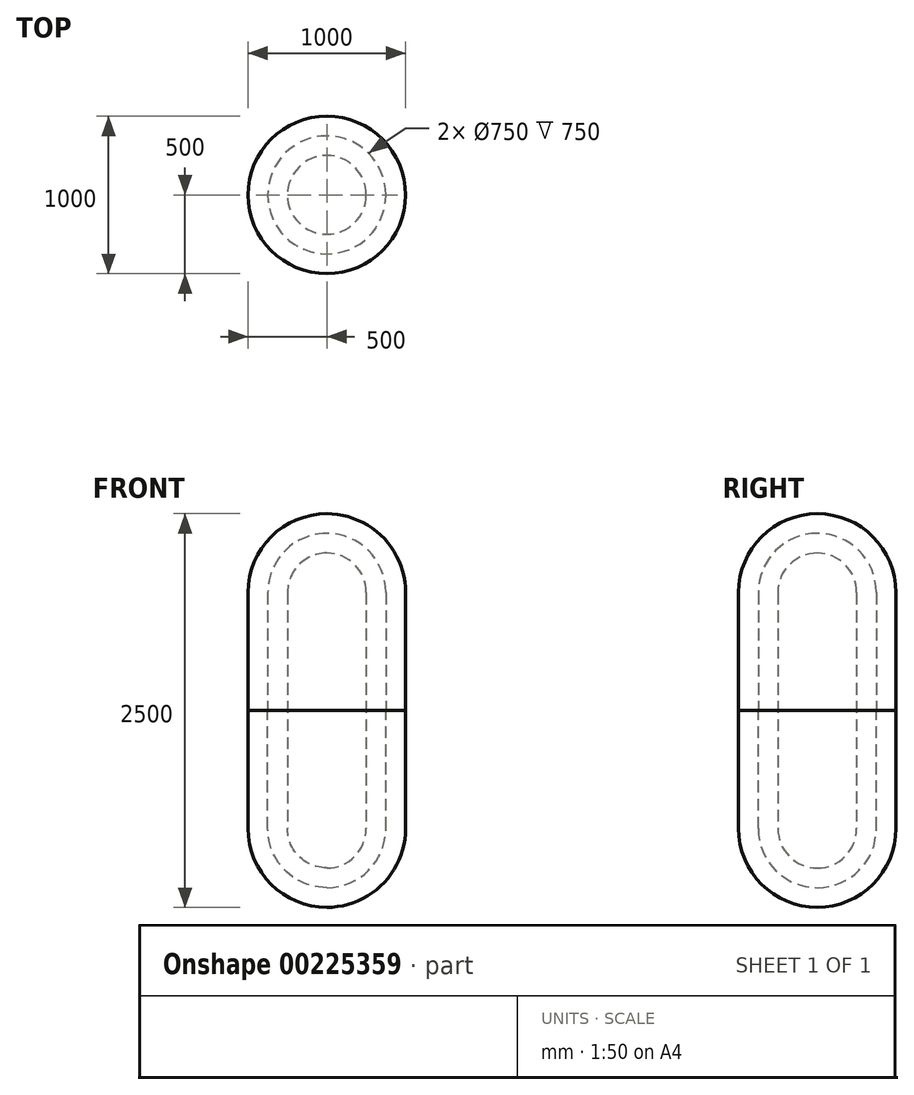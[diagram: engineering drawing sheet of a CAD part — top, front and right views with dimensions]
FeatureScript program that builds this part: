
annotation { "Feature Type Name" : "Feature", "Feature Type Description" : "" }
export const myFeature = defineFeature(function(context is Context, id is Id, definition is map)
    precondition{}
    {
        {
            var Q0;
            Q0=qCreatedBy(makeId("Front.planeOp"),FACE);
            var sketch = newSketch(context, id + "F0", { "sketchPlane" : qUnion([Q0])});
            skLineSegment(sketch, "E0", {"start": v(0, 0) * mm, "end": v(0, 1000) * mm});
            skLineSegment(sketch, "E1", {"start": v(0, 0) * mm, "end": v(-250, 0) * mm});
            skPoint(sketch, "E2", {"position": v(0, 750) * mm});
            skArc(sketch, "E3", {"start": v(0, 1000) * mm, "mid": v(-176.78, 926.78) * mm, "end": v(-250, 750) * mm});
            skLineSegment(sketch, "E4", {"start": v(-250, 0) * mm, "end": v(-250, 750) * mm});
            skSolve(sketch);
        }
        {
            var Q0;
            Q0=qSketchRegion(id+"F0",true);
            var Q1;
            Q1=sQuery(id+"F0.wireOp",EDGE,"E0");
            revolve(context, id + "F1", {"entities" : qUnion([Q0]), "axis" : qUnion([Q1]), "revolveType" : RevolveType.FULL});
        }
        {
            var Q0;
            Q0=makeQuery(id+"F1.opRevolve","SWEPT_BODY",BODY,{"disambiguationData":[OSD([sQuery(id+"F0.wireOp",EDGE,"E0"),sQuery(id+"F0.wireOp",EDGE,"E1"),sQuery(id+"F0.wireOp",EDGE,"E3"),sQuery(id+"F0.wireOp",EDGE,"E4")])]});
            var Q1;
            Q1=makeQuery(id+"F1.opRevolve","SWEPT_FACE",FACE,{"disambiguationData":[OSD([sQuery(id+"F0.wireOp",EDGE,"E1")])]});
            mirror(context, id + "F2", {"operationType" : NewBodyOperationType.ADD, "entities" : qUnion([Q0]), "mirrorPlane" : qUnion([Q1])});
        }
        {
            var Q0;
            Q0=qCreatedBy(makeId("Front.planeOp"),FACE);
            var sketch = newSketch(context, id + "F3", { "sketchPlane" : qUnion([Q0])});
            skLineSegment(sketch, "E5", {"start": v(-375, 0) * mm, "end": v(-500, 0) * mm});
            skPoint(sketch, "E6", {"position": v(0, 750) * mm});
            skArc(sketch, "E7", {"start": v(0, 1250) * mm, "mid": v(-353.55, 1103.55) * mm, "end": v(-500, 750) * mm});
            skLineSegment(sketch, "E8", {"start": v(-500, 0) * mm, "end": v(-500, 750) * mm});
            skArc(sketch, "E9", {"start": v(0, 1125) * mm, "mid": v(-265.17, 1015.17) * mm, "end": v(-375, 750) * mm});
            skLineSegment(sketch, "E10.trimOffspring", {"start": v(0, 1125) * mm, "end": v(0, 1250) * mm});
            skLineSegment(sketch, "E11", {"start": v(-375, 750) * mm, "end": v(-375, 0) * mm});
            skSolve(sketch);
        }
        {
            var Q0;
            Q0=qSketchRegion(id+"F3",true);
            var Q1;
            Q1=sQuery(id+"F3.wireOp",EDGE,"E10.trimOffspring");
            revolve(context, id + "F4", {"entities" : qUnion([Q0]), "axis" : qUnion([Q1]), "revolveType" : RevolveType.FULL});
        }
        {
            var Q0;
            Q0=makeQuery(id+"F4.opRevolve","SWEPT_BODY",BODY,{"disambiguationData":[OSD([sQuery(id+"F3.wireOp",EDGE,"E5"),sQuery(id+"F3.wireOp",EDGE,"E7"),sQuery(id+"F3.wireOp",EDGE,"E8"),sQuery(id+"F3.wireOp",EDGE,"E9"),sQuery(id+"F3.wireOp",EDGE,"E10.trimOffspring"),sQuery(id+"F3.wireOp",EDGE,"E11")])]});
            var Q1;
            Q1=makeQuery(id+"F4.opRevolve","SWEPT_FACE",FACE,{"disambiguationData":[OSD([sQuery(id+"F3.wireOp",EDGE,"E5")])]});
            mirror(context, id + "F5", {"operationType" : NewBodyOperationType.ADD, "entities" : qUnion([Q0]), "mirrorPlane" : qUnion([Q1])});
        }
    });
